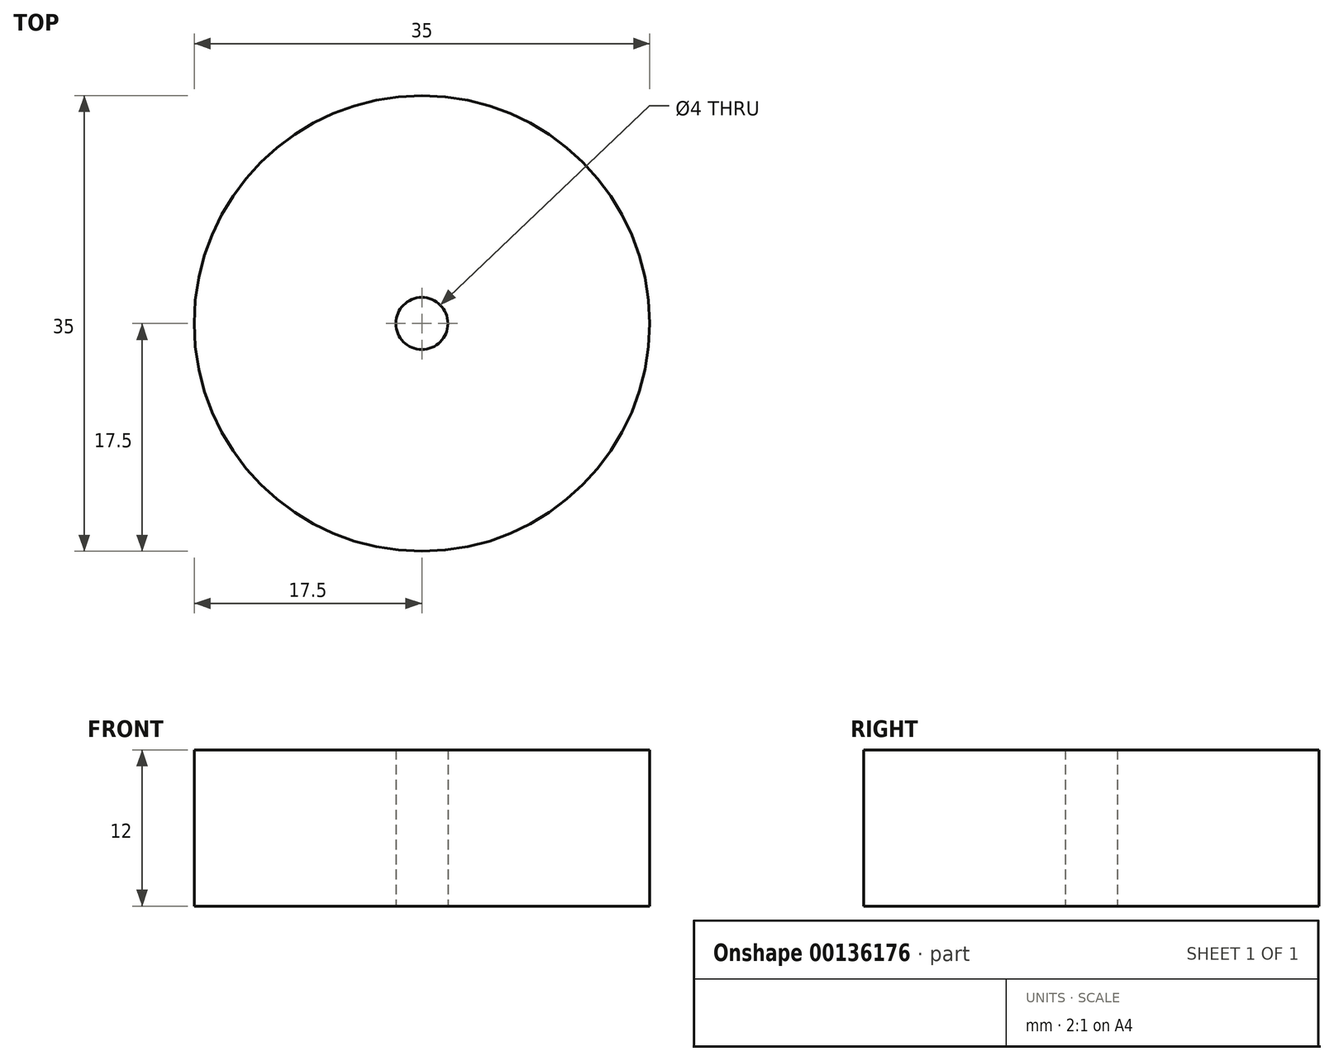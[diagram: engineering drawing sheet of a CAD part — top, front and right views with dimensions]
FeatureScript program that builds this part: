
annotation { "Feature Type Name" : "Feature", "Feature Type Description" : "" }
export const myFeature = defineFeature(function(context is Context, id is Id, definition is map)
    precondition{}
    {
        {
            var Q0;
            Q0=qCreatedBy(makeId("Top.planeOp"),FACE);
            var sketch = newSketch(context, id + "F0", { "sketchPlane" : qUnion([Q0])});
            skCircle(sketch, "E0", {"center": v(0, 0) * mm, "radius": 17.5 * mm});
            skCircle(sketch, "E1", {"center": v(0, 0) * mm, "radius": 2 * mm});
            skSolve(sketch);
        }
        {
            var Q0;
            Q0 = qSketchRegion(id + "F0", true);
            extrude(context, id + "F1", {"entities" : qUnion([Q0]), "depth" : 12 * mm});
        }
    });
